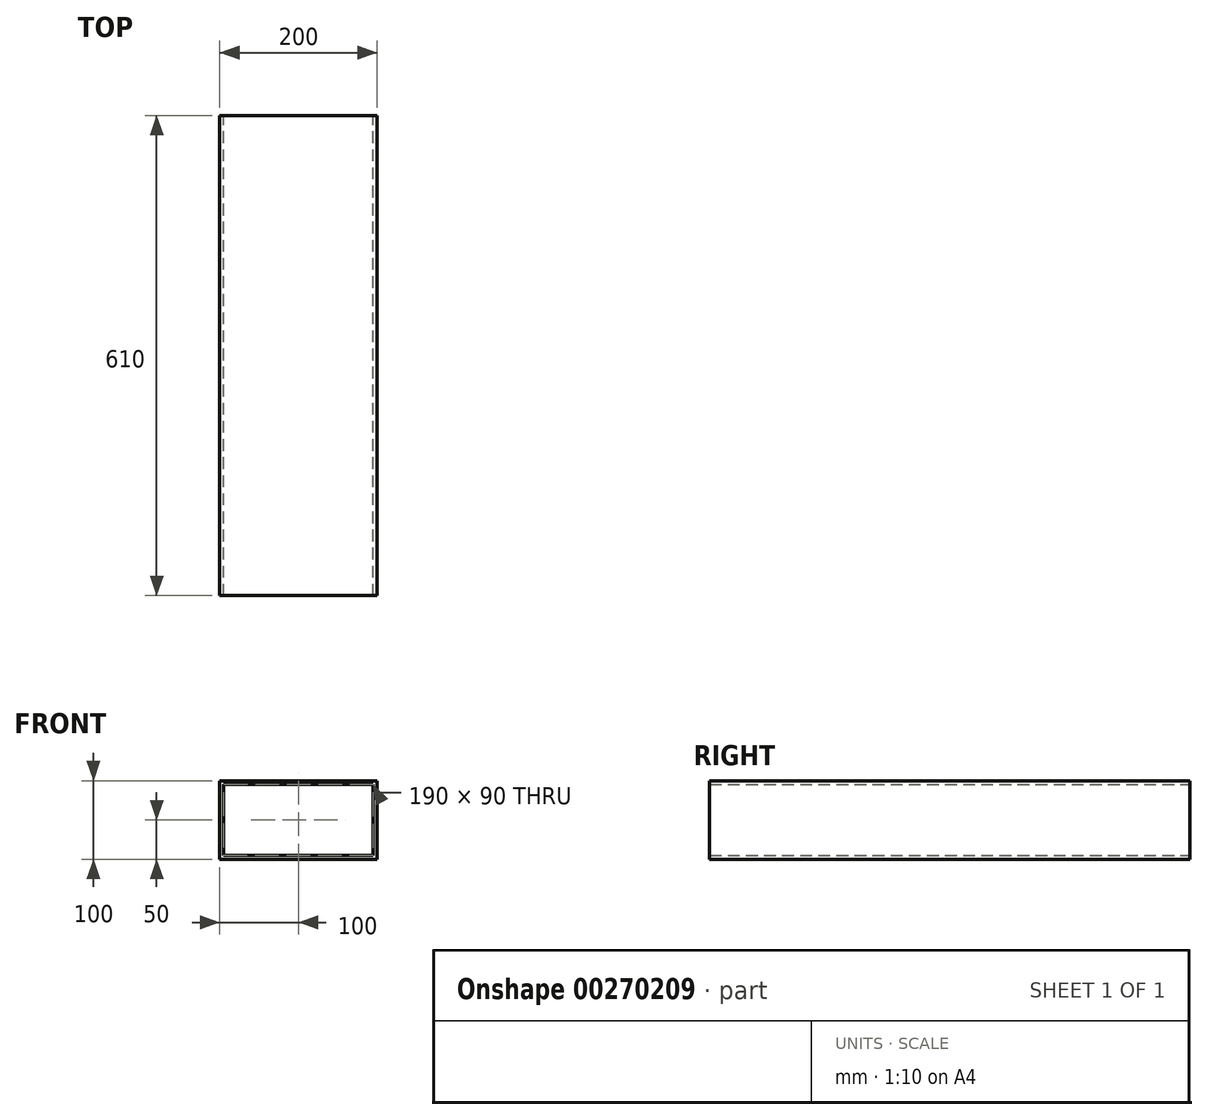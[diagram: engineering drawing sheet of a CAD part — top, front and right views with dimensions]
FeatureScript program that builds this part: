
annotation { "Feature Type Name" : "Feature", "Feature Type Description" : "" }
export const myFeature = defineFeature(function(context is Context, id is Id, definition is map)
    precondition{}
    {
        {
            var Q0;
            Q0=qCreatedBy(makeId("Front.planeOp"),FACE);
            var sketch = newSketch(context, id + "F0", { "sketchPlane" : qUnion([Q0])});
            skLineSegment(sketch, "E0.bottom", {"start": v(100, -50) * mm, "end": v(-100, -50) * mm});
            skLineSegment(sketch, "E0.top", {"start": v(100, 50) * mm, "end": v(-100, 50) * mm});
            skLineSegment(sketch, "E0.left", {"start": v(100, -50) * mm, "end": v(100, 50) * mm});
            skLineSegment(sketch, "E0.right", {"start": v(-100, -50) * mm, "end": v(-100, 50) * mm});
            skPoint(sketch, "E0.middle", {"position": v(0, 0) * mm});
            skLineSegment(sketch, "E1.bottom", {"start": v(95, -45) * mm, "end": v(-95, -45) * mm});
            skLineSegment(sketch, "E1.top", {"start": v(95, 45) * mm, "end": v(-95, 45) * mm});
            skLineSegment(sketch, "E1.left", {"start": v(95, -45) * mm, "end": v(95, 45) * mm});
            skLineSegment(sketch, "E1.right", {"start": v(-95, -45) * mm, "end": v(-95, 45) * mm});
            skSolve(sketch);
        }
        {
            var Q0;
            Q0=makeQuery(id+"F0.imprint","IMPRINT",FACE,{"disambiguationData":[TD([[makeQuery(id+"F0.imprint","IMPRINT",EDGE,{"derivedFrom":sQuery(id+"F0.wireOp",EDGE,"E0.bottom")}),-1.0]])]});
            extrude(context, id + "F1", {"entities" : qUnion([Q0]), "depth" : 610 * mm});
        }
    });
